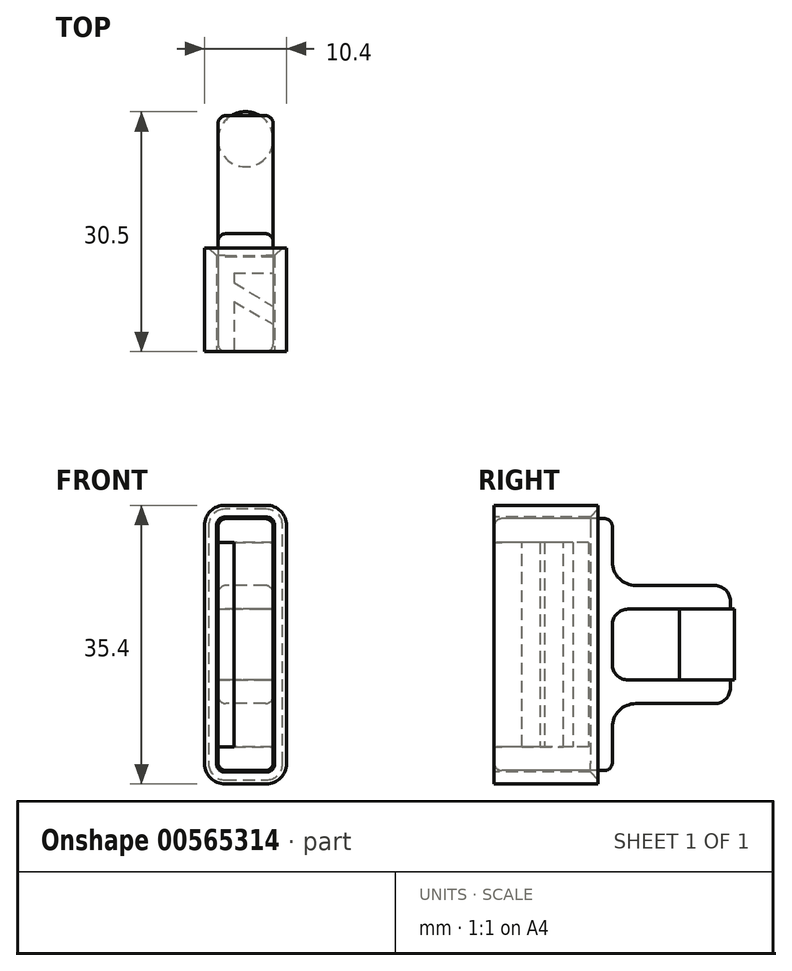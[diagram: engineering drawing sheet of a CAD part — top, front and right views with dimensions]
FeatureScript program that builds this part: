
annotation { "Feature Type Name" : "Feature", "Feature Type Description" : "" }
export const myFeature = defineFeature(function(context is Context, id is Id, definition is map)
    precondition{}
    {
        {
            var Q0;
            Q0=qCreatedBy(makeId("Right.planeOp"),FACE);
            var sketch = newSketch(context, id + "F0", { "sketchPlane" : qUnion([Q0])});
            skLineSegment(sketch, "E0.bottom", {"start": v(3, 4.5) * mm, "end": v(-12, 4.5) * mm});
            skLineSegment(sketch, "E0.top", {"start": v(3, 7.5) * mm, "end": v(-12, 7.5) * mm});
            skLineSegment(sketch, "E0.left", {"start": v(3, 4.5) * mm, "end": v(3, 7.5) * mm});
            skLineSegment(sketch, "E0.right", {"start": v(-12, 4.5) * mm, "end": v(-12, 7.5) * mm});
            skLineSegment(sketch, "E1.bottom", {"start": v(3, -4.5) * mm, "end": v(-12, -4.5) * mm});
            skLineSegment(sketch, "E1.top", {"start": v(3, -7.5) * mm, "end": v(-12, -7.5) * mm});
            skLineSegment(sketch, "E1.left", {"start": v(3, -4.5) * mm, "end": v(3, -7.5) * mm});
            skLineSegment(sketch, "E1.right", {"start": v(-12, -4.5) * mm, "end": v(-12, -7.5) * mm});
            skLineSegment(sketch, "E2.bottom", {"start": v(-12, 16) * mm, "end": v(-27, 16) * mm});
            skLineSegment(sketch, "E2.top", {"start": v(-12, -16) * mm, "end": v(-27, -16) * mm});
            skLineSegment(sketch, "E2.left", {"start": v(-12, 16) * mm, "end": v(-12, -16) * mm});
            skLineSegment(sketch, "E2.right", {"start": v(-27, 16) * mm, "end": v(-27, -16) * mm});
            skLineSegment(sketch, "E3.bottom", {"start": v(-15, 13) * mm, "end": v(-19.5, 13) * mm});
            skLineSegment(sketch, "E3.top", {"start": v(-15, -13) * mm, "end": v(-19.5, -13) * mm});
            skLineSegment(sketch, "E3.left", {"start": v(-15, 13) * mm, "end": v(-15, -13) * mm});
            skLineSegment(sketch, "E3.right", {"start": v(-19.5, 13) * mm, "end": v(-19.5, -13) * mm});
            skPoint(sketch, "E4", {"position": v(-12, 0) * mm});
            skPoint(sketch, "E5", {"position": v(-15, 0) * mm});
            skLineSegment(sketch, "E6", {"start": v(0, 4.5) * mm, "end": v(0, -4.5) * mm, "construction": true});
            skPoint(sketch, "E7", {"position": v(0, 0) * mm});
            skSolve(sketch);
        }
        {
            var Q0;
            Q0=qSketchRegion(id+"F0",true);
            extrude(context, id + "F1", {"entities" : qUnion([Q0]), "endBound" : BoundingType.SYMMETRIC, "depth" : 7 * mm, "offsetDistance" : 25 * mm});
        }
        {
            var Q0;
            Q0=makeQuery(id+"F1.opExtrude","SWEPT_FACE",FACE,{"disambiguationData":[OSD([sQuery(id+"F0.wireOp",EDGE,"E1.bottom")])]});
            var sketch = newSketch(context, id + "F2", { "sketchPlane" : qUnion([Q0])});
            skCircle(sketch, "E8", {"center": v(0, 0) * mm, "radius": 3.5 * mm});
            skSolve(sketch);
        }
        {
            var Q0;
            Q0=qSketchRegion(id+"F2",true);
            var Q1;
            Q1=makeQuery(id+"F1.opExtrude","SWEPT_FACE",FACE,{"disambiguationData":[OSD([sQuery(id+"F0.wireOp",EDGE,"E0.bottom")])]});
            extrude(context, id + "F3", {"entities" : qUnion([Q0]), "operationType" : NewBodyOperationType.ADD, "endBound" : BoundingType.UP_TO_SURFACE, "depth" : 25 * mm, "endBoundEntityFace" : qUnion([Q1]), "offsetDistance" : 25 * mm});
        }
        {
            var Q0;
            Q0=makeQuery(id+"F1.opExtrude","SWEPT_EDGE",EDGE,{"disambiguationData":[OSD([sQuery(id+"F0.wireOp",EDGE,"E2.bottom"),sQuery(id+"F0.wireOp",EDGE,"E2.left")])]});
            var Q1;
            Q1=makeQuery(id+"F1.opExtrude","SWEPT_EDGE",EDGE,{"disambiguationData":[OSD([sQuery(id+"F0.wireOp",EDGE,"E2.top"),sQuery(id+"F0.wireOp",EDGE,"E2.left")])]});
            var Q2;
            Q2=makeQuery(id+"F1.opExtrude","SWEPT_EDGE",EDGE,{"disambiguationData":[OSD([sQuery(id+"F0.wireOp",EDGE,"E2.bottom"),sQuery(id+"F0.wireOp",EDGE,"E2.right")])]});
            var Q3;
            Q3=makeQuery(id+"F1.opExtrude","SWEPT_EDGE",EDGE,{"disambiguationData":[OSD([sQuery(id+"F0.wireOp",EDGE,"E2.top"),sQuery(id+"F0.wireOp",EDGE,"E2.right")])]});
            fillet(context, id + "F4", {"entities" : qUnion([Q0, Q1, Q2, Q3]), "radius" : 1 * mm, "tangentPropagation" : true, "allowEdgeOverflow" : false});
        }
        {
            var Q0;
            Q0=makeQuery(id+"F1.opExtrude","SWEPT_EDGE",EDGE,{"disambiguationData":[OSD([sQuery(id+"F0.wireOp",EDGE,"E0.top"),sQuery(id+"F0.wireOp",EDGE,"E2.left")])]});
            var Q1;
            Q1=makeQuery(id+"F1.opExtrude","SWEPT_EDGE",EDGE,{"disambiguationData":[OSD([sQuery(id+"F0.wireOp",EDGE,"E1.top"),sQuery(id+"F0.wireOp",EDGE,"E2.left")])]});
            fillet(context, id + "F5", {"entities" : qUnion([Q0, Q1]), "radius" : 3 * mm, "tangentPropagation" : true, "allowEdgeOverflow" : false});
        }
        {
            var Q0;
            Q0=makeQuery(id+"F1.opExtrude","SWEPT_EDGE",EDGE,{"disambiguationData":[OSD([sQuery(id+"F0.wireOp",EDGE,"E0.top"),sQuery(id+"F0.wireOp",EDGE,"E0.left")])]});
            var Q1;
            Q1=makeQuery(id+"F1.opExtrude","SWEPT_EDGE",EDGE,{"disambiguationData":[OSD([sQuery(id+"F0.wireOp",EDGE,"E1.top"),sQuery(id+"F0.wireOp",EDGE,"E1.left")])]});
            var Q2;
            Q2=makeQuery(id+"F1.opExtrude","SWEPT_EDGE",EDGE,{"disambiguationData":[OSD([sQuery(id+"F0.wireOp",EDGE,"E1.bottom"),sQuery(id+"F0.wireOp",EDGE,"E2.left")])]});
            var Q3;
            Q3=makeQuery(id+"F1.opExtrude","SWEPT_EDGE",EDGE,{"disambiguationData":[OSD([sQuery(id+"F0.wireOp",EDGE,"E0.bottom"),sQuery(id+"F0.wireOp",EDGE,"E2.left")])]});
            fillet(context, id + "F6", {"entities" : qUnion([Q0, Q1, Q2, Q3]), "radius" : 2 * mm, "tangentPropagation" : true, "allowEdgeOverflow" : false});
        }
        {
            var Q0;
            {var subQ0=sQuery(id+"F0.wireOp",EDGE,"E0.left");var subQ1=sQuery(id+"F0.wireOp",EDGE,"E0.top");Q0=makeQuery(id+"F6.opFillet","BLEND_EDGE",EDGE,{"blendedFrom":[makeQuery(id+"F1.opExtrude","SWEPT_EDGE",EDGE,{"disambiguationData":[OSD([subQ1,subQ0])]}),makeQuery(id+"F1.opExtrude","CAP_FACE",FACE,{"disambiguationData":[OSD([sQuery(id+"F0.wireOp",EDGE,"E0.bottom"),subQ1,subQ0,sQuery(id+"F0.wireOp",EDGE,"E1.bottom"),sQuery(id+"F0.wireOp",EDGE,"E1.top"),sQuery(id+"F0.wireOp",EDGE,"E1.left"),sQuery(id+"F0.wireOp",EDGE,"E2.bottom"),sQuery(id+"F0.wireOp",EDGE,"E2.top"),sQuery(id+"F0.wireOp",EDGE,"E2.left"),sQuery(id+"F0.wireOp",EDGE,"E2.right"),sQuery(id+"F0.wireOp",EDGE,"E3.bottom"),sQuery(id+"F0.wireOp",EDGE,"E3.top"),sQuery(id+"F0.wireOp",EDGE,"E3.left"),sQuery(id+"F0.wireOp",EDGE,"E3.right")])],"isStart":false})],"blendedInto":[makeQuery(id+"F1.opExtrude","CAP_FACE",FACE,{"disambiguationData":[OSD([sQuery(id+"F0.wireOp",EDGE,"E0.bottom"),subQ1,subQ0,sQuery(id+"F0.wireOp",EDGE,"E1.bottom"),sQuery(id+"F0.wireOp",EDGE,"E1.top"),sQuery(id+"F0.wireOp",EDGE,"E1.left"),sQuery(id+"F0.wireOp",EDGE,"E2.bottom"),sQuery(id+"F0.wireOp",EDGE,"E2.top"),sQuery(id+"F0.wireOp",EDGE,"E2.left"),sQuery(id+"F0.wireOp",EDGE,"E2.right"),sQuery(id+"F0.wireOp",EDGE,"E3.bottom"),sQuery(id+"F0.wireOp",EDGE,"E3.top"),sQuery(id+"F0.wireOp",EDGE,"E3.left"),sQuery(id+"F0.wireOp",EDGE,"E3.right")])],"isStart":false})]});}
            var Q1;
            {var subQ0=sQuery(id+"F0.wireOp",EDGE,"E1.left");var subQ1=sQuery(id+"F0.wireOp",EDGE,"E1.top");Q1=makeQuery(id+"F6.opFillet","BLEND_EDGE",EDGE,{"blendedFrom":[makeQuery(id+"F1.opExtrude","SWEPT_EDGE",EDGE,{"disambiguationData":[OSD([subQ1,subQ0])]}),makeQuery(id+"F1.opExtrude","CAP_FACE",FACE,{"disambiguationData":[OSD([sQuery(id+"F0.wireOp",EDGE,"E0.bottom"),sQuery(id+"F0.wireOp",EDGE,"E0.top"),sQuery(id+"F0.wireOp",EDGE,"E0.left"),sQuery(id+"F0.wireOp",EDGE,"E1.bottom"),subQ1,subQ0,sQuery(id+"F0.wireOp",EDGE,"E2.bottom"),sQuery(id+"F0.wireOp",EDGE,"E2.top"),sQuery(id+"F0.wireOp",EDGE,"E2.left"),sQuery(id+"F0.wireOp",EDGE,"E2.right"),sQuery(id+"F0.wireOp",EDGE,"E3.bottom"),sQuery(id+"F0.wireOp",EDGE,"E3.top"),sQuery(id+"F0.wireOp",EDGE,"E3.left"),sQuery(id+"F0.wireOp",EDGE,"E3.right")])],"isStart":false})],"blendedInto":[makeQuery(id+"F1.opExtrude","CAP_FACE",FACE,{"disambiguationData":[OSD([sQuery(id+"F0.wireOp",EDGE,"E0.bottom"),sQuery(id+"F0.wireOp",EDGE,"E0.top"),sQuery(id+"F0.wireOp",EDGE,"E0.left"),sQuery(id+"F0.wireOp",EDGE,"E1.bottom"),subQ1,subQ0,sQuery(id+"F0.wireOp",EDGE,"E2.bottom"),sQuery(id+"F0.wireOp",EDGE,"E2.top"),sQuery(id+"F0.wireOp",EDGE,"E2.left"),sQuery(id+"F0.wireOp",EDGE,"E2.right"),sQuery(id+"F0.wireOp",EDGE,"E3.bottom"),sQuery(id+"F0.wireOp",EDGE,"E3.top"),sQuery(id+"F0.wireOp",EDGE,"E3.left"),sQuery(id+"F0.wireOp",EDGE,"E3.right")])],"isStart":false})]});}
            var Q2;
            Q2=makeQuery(id+"F1.opExtrude","CAP_EDGE",EDGE,{"disambiguationData":[OSD([sQuery(id+"F0.wireOp",EDGE,"E2.top")])],"isStart":true});
            var Q3;
            Q3=makeQuery(id+"F1.opExtrude","CAP_EDGE",EDGE,{"disambiguationData":[OSD([sQuery(id+"F0.wireOp",EDGE,"E2.bottom")])],"isStart":true});
            fillet(context, id + "F7", {"entities" : qUnion([Q0, Q1, Q2, Q3]), "radius" : 1 * mm, "tangentPropagation" : true, "allowEdgeOverflow" : false});
        }
        {
            var Q0;
            Q0=makeQuery(id+"F1.opExtrude","CAP_EDGE",EDGE,{"disambiguationData":[OSD([sQuery(id+"F0.wireOp",EDGE,"E3.right")])],"isStart":false});
            chamfer(context, id + "F8", {"entities" : qUnion([Q0]), "chamferType" : ChamferType.TWO_OFFSETS, "width1" : 7 * mm, "oppositeDirection" : false, "width2" : 4 * mm, "tangentPropagation" : true});
        }
        {
            var Q0;
            Q0=makeQuery(id+"F1.opExtrude","CAP_FACE",FACE,{"disambiguationData":[OSD([sQuery(id+"F0.wireOp",EDGE,"E0.bottom"),sQuery(id+"F0.wireOp",EDGE,"E0.top"),sQuery(id+"F0.wireOp",EDGE,"E0.left"),sQuery(id+"F0.wireOp",EDGE,"E1.bottom"),sQuery(id+"F0.wireOp",EDGE,"E1.top"),sQuery(id+"F0.wireOp",EDGE,"E1.left"),sQuery(id+"F0.wireOp",EDGE,"E2.bottom"),sQuery(id+"F0.wireOp",EDGE,"E2.top"),sQuery(id+"F0.wireOp",EDGE,"E2.left"),sQuery(id+"F0.wireOp",EDGE,"E2.right"),sQuery(id+"F0.wireOp",EDGE,"E3.bottom"),sQuery(id+"F0.wireOp",EDGE,"E3.top"),sQuery(id+"F0.wireOp",EDGE,"E3.left"),sQuery(id+"F0.wireOp",EDGE,"E3.right")])],"isStart":false});
            var sketch = newSketch(context, id + "F9", { "sketchPlane" : qUnion([Q0])});
            skLineSegment(sketch, "E9.bottom", {"start": v(-17, 13) * mm, "end": v(-21.2, 13) * mm});
            skLineSegment(sketch, "E9.top", {"start": v(-17, -13) * mm, "end": v(-21.2, -13) * mm});
            skLineSegment(sketch, "E9.left", {"start": v(-17, 13) * mm, "end": v(-17, -13) * mm});
            skLineSegment(sketch, "E9.right", {"start": v(-21.2, 13) * mm, "end": v(-21.2, -13) * mm});
            skSolve(sketch);
        }
        {
            var Q0;
            Q0 = qSketchRegion(id + "F9", true);
            extrude(context, id + "F10", {"entities" : qUnion([Q0]), "oppositeDirection" : true, "depth" : 5 * mm, "offsetDistance" : 25 * mm});
        }
        {
            var Q0;
            Q0=makeQuery(id+"F10.opExtrude","CAP_EDGE",EDGE,{"disambiguationData":[OSD([sQuery(id+"F9.wireOp",EDGE,"E9.right")])],"isStart":false});
            chamfer(context, id + "F11", {"entities" : qUnion([Q0]), "chamferType" : ChamferType.TWO_OFFSETS, "width1" : 4.9 * mm, "oppositeDirection" : false, "width2" : 3 * mm, "tangentPropagation" : true});
        }
        {
            var Q0;
            Q0=makeQuery(id+"F1.opExtrude","CAP_FACE",FACE,{"disambiguationData":[OSD([sQuery(id+"F0.wireOp",EDGE,"E0.bottom"),sQuery(id+"F0.wireOp",EDGE,"E0.top"),sQuery(id+"F0.wireOp",EDGE,"E0.left"),sQuery(id+"F0.wireOp",EDGE,"E1.bottom"),sQuery(id+"F0.wireOp",EDGE,"E1.top"),sQuery(id+"F0.wireOp",EDGE,"E1.left"),sQuery(id+"F0.wireOp",EDGE,"E2.bottom"),sQuery(id+"F0.wireOp",EDGE,"E2.top"),sQuery(id+"F0.wireOp",EDGE,"E2.left"),sQuery(id+"F0.wireOp",EDGE,"E2.right"),sQuery(id+"F0.wireOp",EDGE,"E3.bottom"),sQuery(id+"F0.wireOp",EDGE,"E3.top"),sQuery(id+"F0.wireOp",EDGE,"E3.left"),sQuery(id+"F0.wireOp",EDGE,"E3.right")])],"isStart":true});
            var sketch = newSketch(context, id + "F12", { "sketchPlane" : qUnion([Q0])});
            skLineSegment(sketch, "E10.bottom", {"start": v(19.5, -13) * mm, "end": v(27, -13) * mm});
            skLineSegment(sketch, "E10.top", {"start": v(19.5, 13) * mm, "end": v(27, 13) * mm});
            skLineSegment(sketch, "E10.left", {"start": v(19.5, -13) * mm, "end": v(19.5, 13) * mm});
            skLineSegment(sketch, "E10.right", {"start": v(27, -13) * mm, "end": v(27, 13) * mm});
            skSolve(sketch);
        }
        {
            var Q0;
            Q0 = qSketchRegion(id + "F12", true);
            extrude(context, id + "F13", {"entities" : qUnion([Q0]), "operationType" : NewBodyOperationType.REMOVE, "oppositeDirection" : true, "depth" : 2 * mm, "offsetDistance" : 25 * mm});
        }
        {
            var Q0;
            Q0=makeQuery(id+"F1.opExtrude","SWEPT_BODY",BODY,{"disambiguationData":[OSD([sQuery(id+"F0.wireOp",EDGE,"E0.bottom"),sQuery(id+"F0.wireOp",EDGE,"E0.top"),sQuery(id+"F0.wireOp",EDGE,"E0.left"),sQuery(id+"F0.wireOp",EDGE,"E1.bottom"),sQuery(id+"F0.wireOp",EDGE,"E1.top"),sQuery(id+"F0.wireOp",EDGE,"E1.left"),sQuery(id+"F0.wireOp",EDGE,"E2.bottom"),sQuery(id+"F0.wireOp",EDGE,"E2.top"),sQuery(id+"F0.wireOp",EDGE,"E2.left"),sQuery(id+"F0.wireOp",EDGE,"E2.right"),sQuery(id+"F0.wireOp",EDGE,"E3.bottom"),sQuery(id+"F0.wireOp",EDGE,"E3.top"),sQuery(id+"F0.wireOp",EDGE,"E3.left"),sQuery(id+"F0.wireOp",EDGE,"E3.right")])]});
            var Q1;
            Q1=makeQuery(id+"F10.opExtrude","SWEPT_BODY",BODY,{"disambiguationData":[OSD([sQuery(id+"F9.wireOp",EDGE,"E9.bottom"),sQuery(id+"F9.wireOp",EDGE,"E9.top"),sQuery(id+"F9.wireOp",EDGE,"E9.left"),sQuery(id+"F9.wireOp",EDGE,"E9.right")])]});
            booleanBodies(context, id + "F14", {"operationType" : BooleanOperationType.UNION, "tools" : qUnion([Q0, Q1])});
        }
        {
            var Q0;
            Q0=makeQuery(id+"F1.opExtrude","SWEPT_FACE",FACE,{"disambiguationData":[OSD([sQuery(id+"F0.wireOp",EDGE,"E2.right")])]});
            var sketch = newSketch(context, id + "F15", { "sketchPlane" : qUnion([Q0])});
            skLineSegment(sketch, "E11.bottom", {"start": v(2.62, 16.2) * mm, "end": v(-2.62, 16.2) * mm});
            skLineSegment(sketch, "E11.top", {"start": v(2.62, -16.2) * mm, "end": v(-2.62, -16.2) * mm});
            skLineSegment(sketch, "E11.left", {"start": v(3.7, 15.12) * mm, "end": v(3.7, -15.12) * mm});
            skLineSegment(sketch, "E11.right", {"start": v(-3.7, 15.12) * mm, "end": v(-3.7, -15.12) * mm});
            skPoint(sketch, "E11.middle", {"position": v(0, 0) * mm});
            skPoint(sketch, "E12.visualSharp", {"position": v(-3.7, -16.2) * mm});
            skArc(sketch, "E12.filletArc", {"start": v(-3.7, -15.12) * mm, "mid": v(-3.39, -15.89) * mm, "end": v(-2.62, -16.2) * mm});
            skPoint(sketch, "E13.visualSharp", {"position": v(-3.7, 16.2) * mm});
            skArc(sketch, "E13.filletArc", {"start": v(-2.62, 16.2) * mm, "mid": v(-3.39, 15.89) * mm, "end": v(-3.7, 15.12) * mm});
            skPoint(sketch, "E14.visualSharp", {"position": v(3.7, 16.2) * mm});
            skArc(sketch, "E14.filletArc", {"start": v(3.7, 15.12) * mm, "mid": v(3.39, 15.89) * mm, "end": v(2.62, 16.2) * mm});
            skPoint(sketch, "E15.visualSharp", {"position": v(3.7, -16.2) * mm});
            skArc(sketch, "E15.filletArc", {"start": v(2.62, -16.2) * mm, "mid": v(3.39, -15.89) * mm, "end": v(3.7, -15.12) * mm});
            skArc(sketch, "E16.0", {"start": v(-2.62, 17.7) * mm, "mid": v(-4.45, 16.95) * mm, "end": v(-5.2, 15.12) * mm});
            skLineSegment(sketch, "E16.1", {"start": v(2.62, 17.7) * mm, "end": v(-2.62, 17.7) * mm});
            skLineSegment(sketch, "E16.2", {"start": v(-5.2, 15.12) * mm, "end": v(-5.2, -15.12) * mm});
            skArc(sketch, "E16.3", {"start": v(5.2, 15.12) * mm, "mid": v(4.45, 16.95) * mm, "end": v(2.62, 17.7) * mm});
            skArc(sketch, "E16.4", {"start": v(-5.2, -15.12) * mm, "mid": v(-4.45, -16.95) * mm, "end": v(-2.62, -17.7) * mm});
            skLineSegment(sketch, "E16.5", {"start": v(2.62, -17.7) * mm, "end": v(-2.62, -17.7) * mm});
            skArc(sketch, "E16.6", {"start": v(2.62, -17.7) * mm, "mid": v(4.45, -16.95) * mm, "end": v(5.2, -15.12) * mm});
            skLineSegment(sketch, "E16.7", {"start": v(5.2, 15.12) * mm, "end": v(5.2, -15.12) * mm});
            skSolve(sketch);
        }
        {
            var Q0;
            Q0 = qSketchRegion(id + "F15", true);
            extrude(context, id + "F16", {"entities" : qUnion([Q0]), "oppositeDirection" : true, "depth" : 13.2 * mm, "offsetDistance" : 25 * mm});
        }
        {
            var Q0;
            Q0=makeQuery(id+"F16.opExtrude","CAP_EDGE",EDGE,{"disambiguationData":[OSD([sQuery(id+"F15.wireOp",EDGE,"E11.right")])],"isStart":false});
            chamfer(context, id + "F17", {"entities" : qUnion([Q0]), "width" : 1 * mm, "tangentPropagation" : true});
        }
    });
